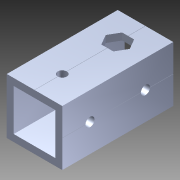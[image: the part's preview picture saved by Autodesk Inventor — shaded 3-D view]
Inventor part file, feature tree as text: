
AUTODESK INVENTOR PART (.ipt)
format: ipt  version: 2014 (Build 180170000, 170)  size: 1,166,848 bytes
history: native  units: in
note: dims shown in document units (in); Inventor stores cm internally (conversion verified against a paired STEP export)
features: extrude x2, sketch x2, pattern_circular x1, other x1, plane x1, imported_body x1
ambient origin geometry x8: Origin, YZ Plane, XZ Plane, XY Plane, X Axis, Y Axis, Z Axis, Center Point
bodies: Body1 (feature_tree)
feature tree (8):
  pattern_circular  "CirPattern2"
  other  "217-3426-STEP1"
  plane  "Work Plane1"
  extrude  "Extrusion1"  Depth=3937.0079in TaperAngle=0.0deg
  extrude  "Extrusion2"  Depth=2.0in TaperAngle=0.0deg
  imported_body  "Base1"
  sketch  "Sketch1"  dims[d0=-2.0in d1=3937.0079in d2=0.0in]
  sketch  "Sketch3"  dims[d3=0.375in d4=2.0in d5=0.0in]
